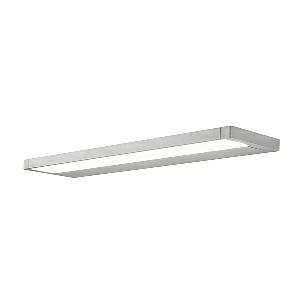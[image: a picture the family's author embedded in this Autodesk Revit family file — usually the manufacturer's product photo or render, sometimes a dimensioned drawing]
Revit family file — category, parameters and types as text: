
# Revit family: zera_wall_-_zew_3000_830_d_00812327_5c1f
name_source: partatom
category: Lighting Fixtures
units: mm (PartAtom-declared; Revit-internal decimal feet)

## family parameters
Cut with Voids When Loaded = No
Host = Face
Light Source = No
Part Type = Normal
Room Calculation Point = No
Round Connector Dimension = Use Diameter
Shared = No

## types (1)
- ZERA.wall - ZEW 3000/830/D (1 x LED, 2800 lm, 3000K)
    Apparent Load = 18 VA
    Approval mark = CE
    CIE Flux Codes = 46 78 95 41 100
    Color Rendering = 80-89
    Color Temperature = 3000K
    Control Gear = Electronic ballast
    Default Elevation = 2000 mm  [stored 6.56168 ft]
    Description = ZEW 3000/830/D|Wall-mounted luminaire|light source:   Warm white   |work equipment: Electronic ballast dimable digital|luminous flux: 2800 lm|light distribution: Direct/indirect|class of protection: I|technology: Continuously dimmable|mains lead: Connector 5 pin|glare control: Diffusor|special features: Asymmetric radiation, DALI Load 1x, DIN EN 60598-2-25, Suitable as emergency lighting|
    Frequency = 50 Hz, 60 Hz
    Height = 29 mm
    Lamp = 1 x LED
    Lamp Light Flux = 2800 lm
    Lamp count = 1
    Length = 550 mm
    Luminous efficacy = 156 lm/W
    Manufacturer = Waldmann
    ModVariant = No
    Model = 00812327
    Mounting Place = Wall
    Mounting Type = Surface mounted
    Number of Poles = 1
    OnlyDefault = Yes
    Power Factor = 1
    Product Name = ZERA.wall - ZEW 3000/830/D
    Product group = Wall mounted Luminaire
    ProductGroupID = 20
    Protection Class = Protection class I
    Protection Degree = IP 20
    RLX_Detail_Level = 1
    RLX_Emergency_Light_Flux = 0 lm
    RLX_Emergency_Type = 0
    RLX_Emergency_Type_DB = No
    RlxData = <blob elided: 36349 chars, md5=51b4a9ef>
    Socket = socket
    Standby Power = 0 W
    System Light Flux = 2800 lm
    System Power = 18 W
    Type Comments = Product without accessories
    Type Image = zera_bath_20_w.jpg
    URL = http://relux.com
    VarID = ---
    Voltage = 230 V
    Voltage Range = 220-240 V
    Weight = 0.00 kg
    Width = 142 mm

note: [stored X ft] marks values corroborated as IEEE doubles in the binary element streams (Revit-internal decimal feet)

## geometry (parser evidence)
native form markers: Blend x4, Sweep x14
no freeform markers — native parametric forms only
